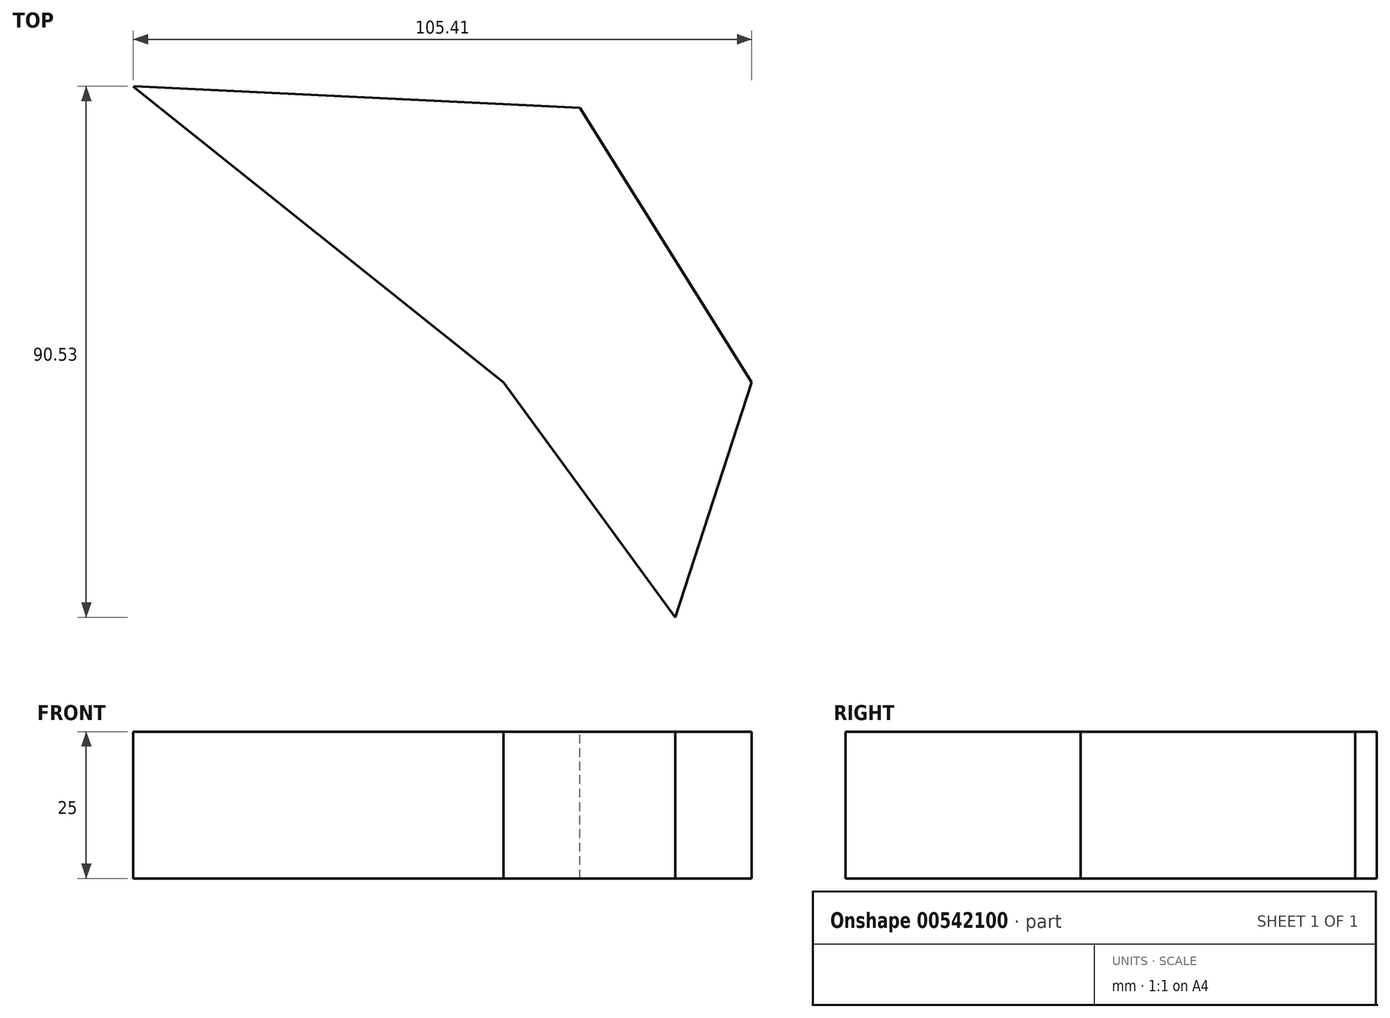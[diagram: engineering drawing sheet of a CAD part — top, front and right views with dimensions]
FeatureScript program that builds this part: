
annotation { "Feature Type Name" : "Feature", "Feature Type Description" : "" }
export const myFeature = defineFeature(function(context is Context, id is Id, definition is map)
    precondition{}
    {
        {
            var Q0;
            Q0=qCreatedBy(makeId("Top.planeOp"),FACE);
            var sketch = newSketch(context, id + "F0", { "sketchPlane" : qUnion([Q0])});
            skLineSegment(sketch, "E0", {"start": v(-49.54, 50.42) * mm, "end": v(13.53, 0) * mm});
            skLineSegment(sketch, "E1", {"start": v(13.53, 0) * mm, "end": v(42.8, -40.06) * mm});
            skLineSegment(sketch, "E2", {"start": v(42.8, -40.06) * mm, "end": v(55.87, 0) * mm});
            skSolve(sketch);
        }
        {
            var Q0;
            Q0=qCreatedBy(makeId("Top.planeOp"),FACE);
            var sketch = newSketch(context, id + "F1", { "sketchPlane" : qUnion([Q0])});
            skLineSegment(sketch, "E3", {"start": v(-49.42, 50.47) * mm, "end": v(26.59, 46.81) * mm});
            skLineSegment(sketch, "E4", {"start": v(26.59, 46.81) * mm, "end": v(55.84, 0) * mm});
            skPoint(sketch, "E5.orphan", {"position": v(55.84, 0) * mm});
            skSolve(sketch);
        }
        {
            var Q0;
            Q0=sQuery(id+"F1.wireOp",EDGE,"E3");
            var Q1;
            Q1=sQuery(id+"F0.wireOp",EDGE,"E0");
            var Q2;
            Q2=sQuery(id+"F1.wireOp",EDGE,"E4");
            var Q3;
            Q3=sQuery(id+"F0.wireOp",EDGE,"E2");
            var Q4;
            Q4=sQuery(id+"F0.wireOp",EDGE,"E1");
            extrude(context, id + "F2", {"bodyType" : ToolBodyType.SURFACE, "surfaceEntities" : qUnion([Q0, Q1, Q2, Q3, Q4]), "depth" : 25 * mm, "offsetDistance" : 25 * mm});
        }
    });
